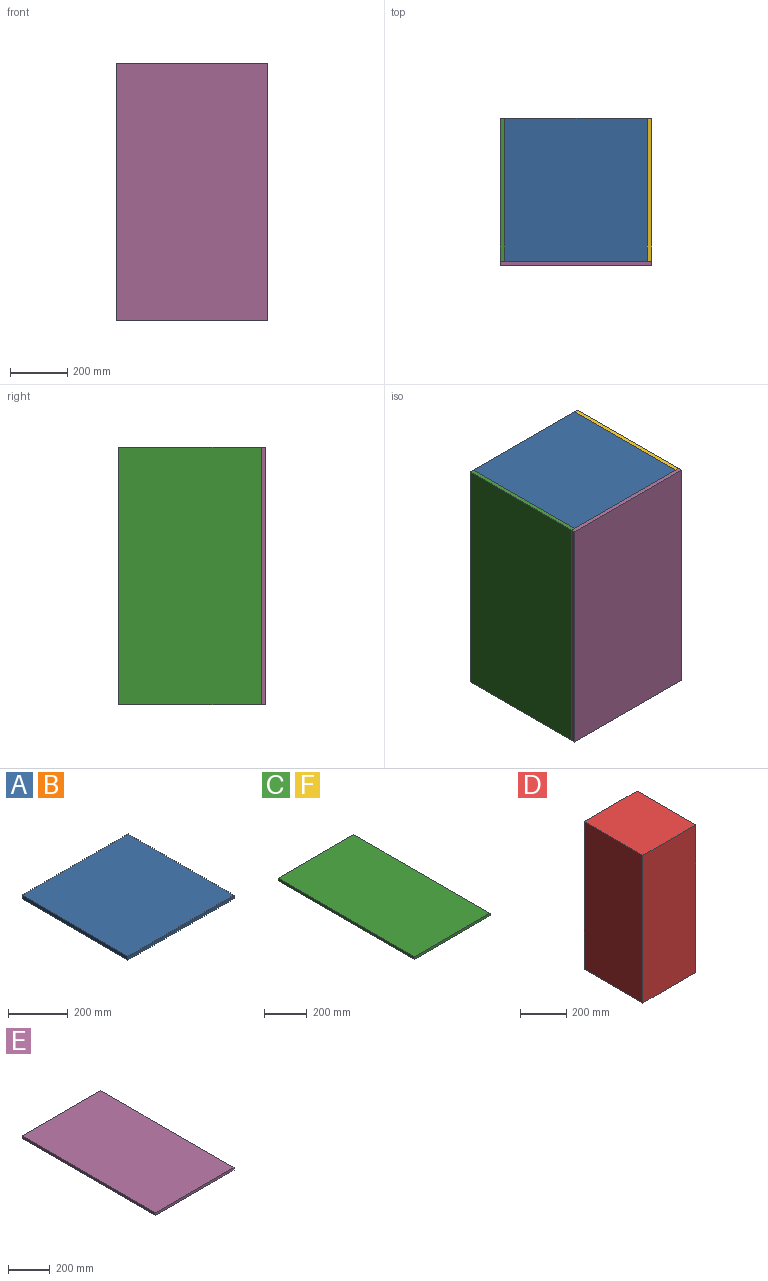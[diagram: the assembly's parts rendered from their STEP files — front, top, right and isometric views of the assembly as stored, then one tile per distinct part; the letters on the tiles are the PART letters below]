
ASSEMBLY  parts=6 mates=5
PART A: 6 faces, bbox 500x500x15 mm
  f0: plane 500x15mm, normal (1,0,0), area 7500mm2, adj f1,f3,f4,f5
  f1: plane 500x15mm, normal (0,1,0), area 7500mm2, adj f0,f2,f4,f5
  f2: plane 500x15mm, normal (-1,0,0), area 7500mm2, adj f1,f3,f4,f5
  f3: plane 500x15mm, normal (0,-1,0), area 7500mm2, adj f0,f2,f4,f5
  f4: plane 500x500mm, normal (0,0,1), area 250000mm2, adj f0,f1,f2,f3
  f5: plane 500x500mm, normal (0,0,-1), area 250000mm2, adj f0,f1,f2,f3
PART B: same geometry as A
PART C: 6 faces, bbox 500x900x15 mm
  f0: plane 900x15mm, normal (1,0,0), area 13500mm2, adj f1,f3,f4,f5
  f1: plane 500x15mm, normal (0,1,0), area 7500mm2, adj f0,f2,f4,f5
  f2: plane 900x15mm, normal (-1,0,0), area 13500mm2, adj f1,f3,f4,f5
  f3: plane 500x15mm, normal (0,-1,0), area 7500mm2, adj f0,f2,f4,f5
  f4: plane 900x500mm, normal (0,0,1), area 450000mm2, adj f0,f1,f2,f3
  f5: plane 900x500mm, normal (0,0,-1), area 450000mm2, adj f0,f1,f2,f3
PART D: 6 faces, bbox 325x360x785 mm
  f0: plane 785x360mm, normal (1,0,0), area 282600mm2, adj f1,f3,f4,f5
  f1: plane 785x325mm, normal (0,1,0), area 255125mm2, adj f0,f2,f4,f5
  f2: plane 785x360mm, normal (-1,0,0), area 282600mm2, adj f1,f3,f4,f5
  f3: plane 785x325mm, normal (0,-1,0), area 255125mm2, adj f0,f2,f4,f5
  f4: plane 360x325mm, normal (0,0,1), area 117000mm2, adj f0,f1,f2,f3
  f5: plane 360x325mm, normal (0,0,-1), area 117000mm2, adj f0,f1,f2,f3
PART E: 6 faces, bbox 530x900x15 mm
  f0: plane 900x15mm, normal (1,0,0), area 13500mm2, adj f1,f3,f4,f5
  f1: plane 530x15mm, normal (0,1,0), area 7950mm2, adj f0,f2,f4,f5
  f2: plane 900x15mm, normal (-1,0,0), area 13500mm2, adj f1,f3,f4,f5
  f3: plane 530x15mm, normal (0,-1,0), area 7950mm2, adj f0,f2,f4,f5
  f4: plane 900x530mm, normal (0,0,1), area 477000mm2, adj f0,f1,f2,f3
  f5: plane 900x530mm, normal (0,0,-1), area 477000mm2, adj f0,f1,f2,f3
PART F: same geometry as C
PLACE A t=(-171.29,-81.07,896.44)mm
PLACE B t=(-171.29,-81.07,11.44)mm
PLACE C rot(axis=(0.58,0.58,0.58),120deg) t=(-436.29,-81.07,461.44)mm
PLACE D rot(axis=(0,0,1),180deg) t=(-186.18,-73.16,26.44)mm
PLACE E rot(axis=(1,0,0),90deg) t=(-171.29,-331.07,461.44)mm
PLACE F rot(axis=(0.58,-0.58,-0.58),120deg) t=(93.71,-81.07,461.44)mm
MATE fastened F.f4 <-> B.f0  axis (-1,0,0) through (78.71,-331.07,11.44)mm
MATE fastened E.f5 <-> F.f0  axis (0,1,0) through (93.71,-331.07,11.44)mm
MATE fastened A.f0 <-> F.f4  axis (1,0,0) through (78.71,168.93,911.44)mm
MATE planar D.f5 <-> B.f4  axis (0,0,-1) through (-186.18,-73.16,26.44)mm
MATE fastened C.f4 <-> B.f2  axis (1,0,0) through (-421.29,-331.07,11.44)mm
